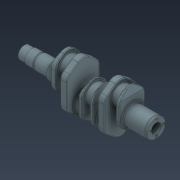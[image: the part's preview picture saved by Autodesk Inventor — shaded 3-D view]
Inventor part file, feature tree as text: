
AUTODESK INVENTOR PART (.ipt)
format: ipt  version: 2022 (Build 260153000, 153)  size: 982,528 bytes
history: native  units: mm
features: sketch x21, extrude x17, plane x4, hole x3, chamfer x3, projected_geometry x3, revolve x2, fillet x2, mirror x2
ambient origin geometry x8: Origin, YZ Plane, XZ Plane, XY Plane, X Axis, Y Axis, Z Axis, Center Point
bodies: Solid1 (feature_tree)
feature tree (57):
  revolve  "Revolution1"  [1 undecoded]
  plane  "Work Plane7"
  sketch  "Sketch22"  dims[d3=44.0mm d4=36.0mm]
  extrude  "Extrusion18"  Depth=36.0mm
  extrude  "Extrusion19"  Depth=42.0mm
  extrude  "Extrusion20"  Depth=2.0mm
  extrude  "Extrusion21"  TaperAngle=90.0deg  [1 undecoded]
  plane  "Work Plane8"
  extrude  "Extrusion22"  Depth=1.0mm
  extrude  "Extrusion23"  Depth=65.0mm
  extrude  "Extrusion24"  Depth=34.5mm
  extrude  "Extrusion25"  Depth=1.0mm TaperAngle=0.0deg
  extrude  "Extrusion26"  Depth=74.0mm
  extrude  "Extrusion27"  Depth=51.2mm
  extrude  "Extrusion28"  Depth=10.0mm TaperAngle=0.0deg
  plane  "Work Plane9"
  extrude  "Extrusion29"  Depth=1.0mm
  extrude  "Extrusion30"  Depth=1.0mm
  fillet  "Fillet1"  Radius=1.0mm
  mirror  "Mirror1"
  mirror  "Mirror2"
  plane  "Work Plane10"
  extrude  "Extrusion32"  Depth=29.9mm
  extrude  "Extrusion33"  Depth=1.0mm TaperAngle=0.0deg
  extrude  "Extrusion34"  Depth=2.0mm
  extrude  "Extrusion35"  Depth=21.0mm TaperAngle=0.0deg
  fillet  "Fillet2"  Radius=1.0mm
  revolve  "Revolution2"  [1 undecoded]
  hole  "Hole1"  [1 undecoded]
  hole  "Hole2"  [1 undecoded]
  hole  "Hole3"  [1 undecoded]
  chamfer  "Chamfer1"  Distance=55.0mm
  chamfer  "Chamfer2"  Distance=21.0mm
  chamfer  "Chamfer3"  Distance=28.965484mm
  sketch  "Sketch1"  dims[d1=23.0mm d2=23.0mm]
  sketch  "Sketch23"  dims[d6=40.0mm d7=42.0mm]
  sketch  "Sketch24"  dims[d9=25.5mm d10=2.0mm]
  sketch  "Sketch25"  dims[d11=1.5mm d12=90.0deg]
  sketch  "Sketch26"  dims[d13=65.0mm d15=1.0mm]
  sketch  "Sketch27"  dims[d96=14.76mm d97=65.0mm]
  sketch  "Sketch28"  dims[d98=55.0mm d99=34.5mm]
  sketch  "Sketch29"  dims[d100=22.0mm d101=0.0mm d102=1.0mm d103=0.0mm]
  sketch  "Sketch30"  dims[d105=15.0mm d106=74.0mm]
  projected_geometry  "Projected Loop9"
  sketch  "Sketch31"  dims[d107=27.2mm d108=51.2mm]
  sketch  "Sketch32"  dims[d109=2.0mm d110=10.0mm d111=0.0mm]
  sketch  "Sketch33"  dims[d112=1.0mm d113=0.0mm d114=18.91mm]
  sketch  "Sketch35"  dims[d115=65.0mm d116=69.0mm d117=1.0mm d118=0.0mm]
  sketch  "Sketch36"  dims[d119=25.0mm d120=29.9mm]
  sketch  "Sketch37"  dims[d122=95.0mm d124=1.0mm d125=0.0mm]
  sketch  "Sketch39"  dims[d126=2.0mm d127=2.0mm]
  projected_geometry  "Projected Loop12"
  projected_geometry  "Projected Loop13"
  sketch  "Sketch40"  dims[d128=55.0mm d129=21.0mm d130=0.0mm d131=1.0mm d132=0.0mm]
  sketch  "Sketch41"  dims[d133=15.0mm d134=25.0mm]
  sketch  "Sketch42"  dims[d135=40.4mm d136=25.0mm]
  sketch  "Sketch43"  dims[d137=10.43mm d138=0.0mm d139=65.0mm d140=1.0mm d141=0.0mm d142=55.0mm d143=21.0mm d144=0.0mm d145=28.965484mm d146=23.0mm d147=0.0mm d148=0.0mm d149=28.965484mm d150=8.0mm d151=10.0mm d152=0.0mm d153=2.0mm d156=10.27mm d157=70.0mm d158=1.0mm d159=0.0mm d160=1.0mm d161=0.0mm d162=28.965484mm d163=23.0mm d164=10.0mm d165=0.0mm d166=0.0mm d167=0.0mm d168=2.0mm d171=53.0mm d172=50.0mm d173=2.0mm d175=21.0mm d176=100.0mm d177=55.0mm d178=68.118mm d179=2.0mm d180=58.0mm d181=3.0mm d182=2.0mm d183=5.0mm d184=90.0deg d185=17.294mm d186=30.7mm d187=20.4mm d188=4.0mm d189=90.0deg d190=30.7mm d191=20.594885mm d192=25.834936mm d193=21.5mm d194=28.3mm d195=5.75mm d196=90.0deg d197=21.5mm d198=20.594885mm d199=1.0mm d200=2.0mm d201=45.0deg d202=1.5mm d203=2.0mm d204=45.0deg d205=2.0mm d206=2.0mm d207=45.0deg d208=41.0mm d209=8.0mm d210=21.5mm d211=28.3mm d212=5.75mm d213=90.0deg d214=12.4mm d215=20.594885mm d41=0.5mm d42=0.872665mm d43=0.5mm d44=0.872665mm d91=0.5mm d92=0.872665mm d93=0.5mm d94=0.872665mm]
note: 6 required parameter values undecoded (feature->parameter linkage not recoverable at this tier; creation-order binding heuristic only, values carry confidence <= 0.55)